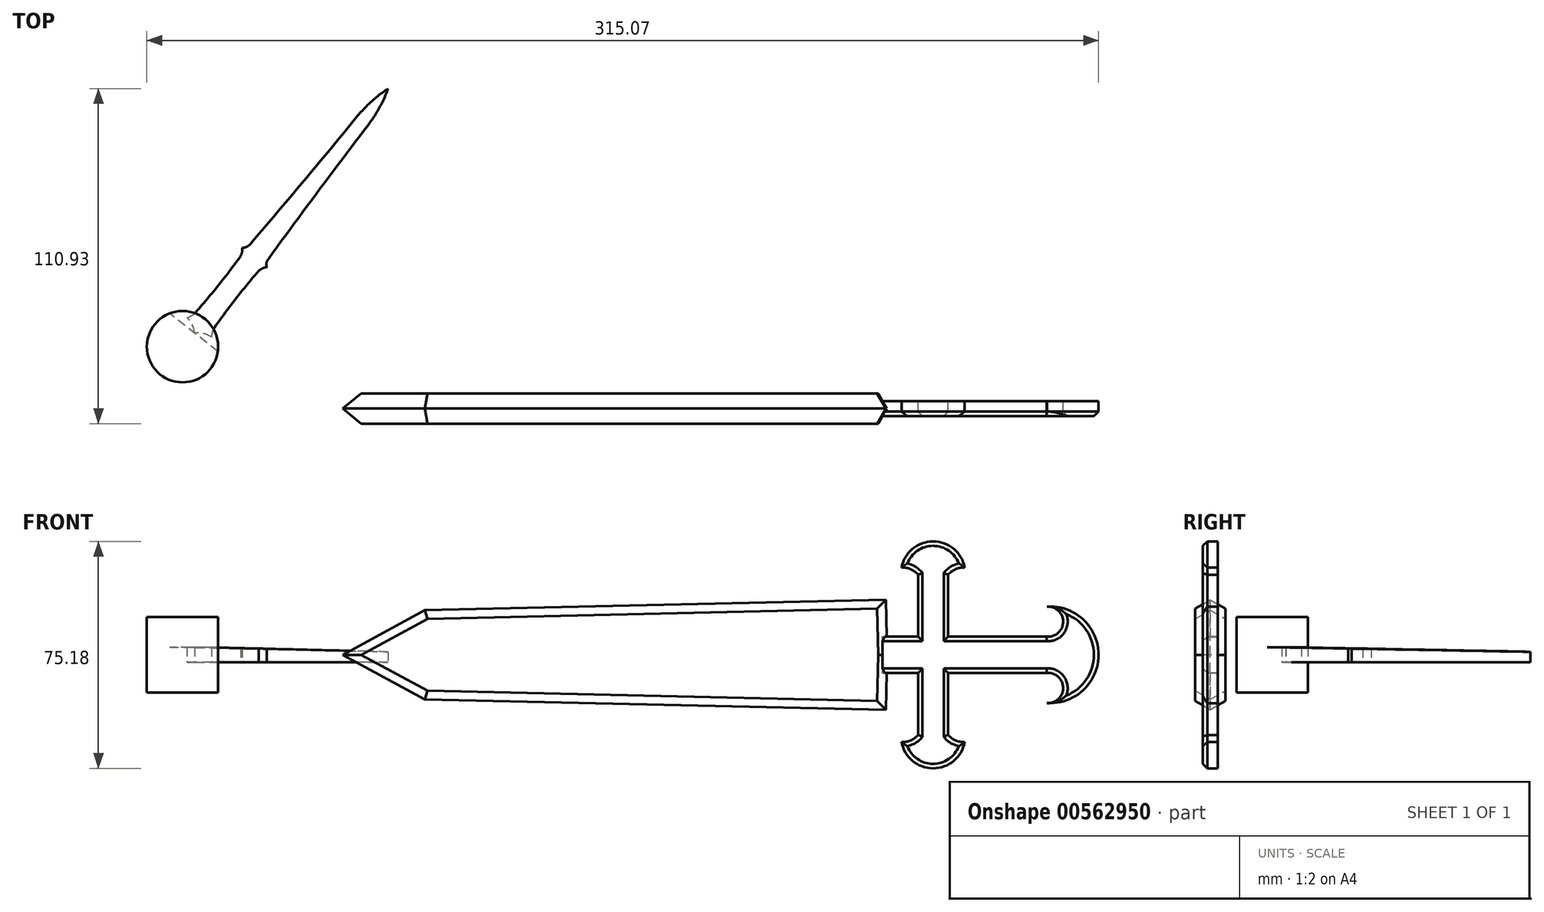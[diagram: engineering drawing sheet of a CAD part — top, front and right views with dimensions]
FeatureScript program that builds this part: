
annotation { "Feature Type Name" : "Feature", "Feature Type Description" : "" }
export const myFeature = defineFeature(function(context is Context, id is Id, definition is map)
    precondition{}
    {
        {
            var Q0;
            Q0=qCreatedBy(makeId("Front.planeOp"),FACE);
            var sketch = newSketch(context, id + "F0", { "sketchPlane" : qUnion([Q0])});
            skLineSegment(sketch, "E0", {"start": v(0, 0) * mm, "end": v(250, 0) * mm, "construction": true});
            skLineSegment(sketch, "E1", {"start": v(0, 0) * mm, "end": v(27.2, 14.78) * mm});
            skLineSegment(sketch, "E2", {"start": v(27.2, 14.78) * mm, "end": v(179.74, 18.21) * mm});
            skLineSegment(sketch, "E3", {"start": v(179.74, 18.21) * mm, "end": v(180.15, 0) * mm});
            skLineSegment(sketch, "E4.MirrorCS", {"start": v(0, 0) * mm, "end": v(27.2, -14.78) * mm});
            skLineSegment(sketch, "E5.MirrorCS", {"start": v(27.2, -14.78) * mm, "end": v(179.74, -18.21) * mm});
            skLineSegment(sketch, "E6.MirrorCS", {"start": v(179.74, -18.21) * mm, "end": v(180.15, 0) * mm});
            skSolve(sketch);
        }
        {
            var Q0;
            Q0=makeQuery(id+"F0.imprint","IMPRINT",FACE,{"disambiguationData":[TD([[makeQuery(id+"F0.imprint","IMPRINT",EDGE,{"derivedFrom":sQuery(id+"F0.wireOp",EDGE,"E1")}),-1.0]])]});
            extrude(context, id + "F1", {"entities" : qUnion([Q0]), "endBound" : BoundingType.SYMMETRIC, "depth" : 10 * mm, "offsetDistance" : 25 * mm, "hasDraft" : true, "draftAngle" : 30 * degree, "draftPullDirection" : true});
        }
        {
            var Q0;
            Q0=qCreatedBy(makeId("Front.planeOp"),FACE);
            var sketch = newSketch(context, id + "F2", { "sketchPlane" : qUnion([Q0])});
            skLineSegment(sketch, "E7", {"start": v(0, 0) * mm, "end": v(460.23, 0) * mm, "construction": true});
            skLineSegment(sketch, "E8", {"start": v(177.13, 6) * mm, "end": v(190.4, 6) * mm});
            skLineSegment(sketch, "E9", {"start": v(190.4, 6) * mm, "end": v(190.4, 26.53) * mm});
            skLineSegment(sketch, "E10", {"start": v(200.4, 26.53) * mm, "end": v(200.4, 6) * mm});
            skLineSegment(sketch, "E11", {"start": v(200.4, 6) * mm, "end": v(233.04, 6) * mm});
            skLineSegment(sketch, "E12", {"start": v(190.4, 6) * mm, "end": v(200.4, 6) * mm, "construction": true});
            skLineSegment(sketch, "E13", {"start": v(195.4, 6) * mm, "end": v(195.4, 44.93) * mm, "construction": true});
            skArc(sketch, "E14", {"start": v(190.4, 26.53) * mm, "mid": v(187.95, 28.36) * mm, "end": v(184.94, 28.88) * mm});
            skArc(sketch, "E15", {"start": v(195.4, 37.6) * mm, "mid": v(188.6, 35.13) * mm, "end": v(184.94, 28.88) * mm});
            skLineSegment(sketch, "E16", {"start": v(195.4, 37.6) * mm, "end": v(213.75, 37.6) * mm, "construction": true});
            skArc(sketch, "E17.MirrorCS", {"start": v(195.4, 37.6) * mm, "mid": v(202.22, 35.13) * mm, "end": v(205.88, 28.88) * mm});
            skArc(sketch, "E18.MirrorCS", {"start": v(200.4, 26.53) * mm, "mid": v(202.86, 28.36) * mm, "end": v(205.88, 28.88) * mm});
            skArc(sketch, "E19", {"start": v(233.04, 6) * mm, "mid": v(238.45, 10.94) * mm, "end": v(233.13, 15.97) * mm});
            skArc(sketch, "E20", {"start": v(250.17, 0) * mm, "mid": v(245.1, 11.68) * mm, "end": v(233.13, 15.97) * mm});
            skLineSegment(sketch, "E21", {"start": v(250.17, 0) * mm, "end": v(250.17, -32.65) * mm, "construction": true});
            skArc(sketch, "E22.MirrorCS", {"start": v(233.04, -6) * mm, "mid": v(238.45, -10.94) * mm, "end": v(233.13, -15.97) * mm});
            skArc(sketch, "E23.MirrorCS", {"start": v(250.17, 0) * mm, "mid": v(245.1, -11.68) * mm, "end": v(233.13, -15.97) * mm});
            skLineSegment(sketch, "E24.MirrorCS", {"start": v(200.4, -6) * mm, "end": v(233.04, -6) * mm});
            skLineSegment(sketch, "E25.MirrorCS", {"start": v(200.4, -26.53) * mm, "end": v(200.4, -6) * mm});
            skArc(sketch, "E26.MirrorCS", {"start": v(200.4, -26.53) * mm, "mid": v(202.86, -28.36) * mm, "end": v(205.88, -28.88) * mm});
            skArc(sketch, "E27.MirrorCS", {"start": v(195.4, -37.6) * mm, "mid": v(202.22, -35.13) * mm, "end": v(205.88, -28.88) * mm});
            skArc(sketch, "E28.MirrorCS", {"start": v(195.4, -37.6) * mm, "mid": v(188.6, -35.13) * mm, "end": v(184.94, -28.88) * mm});
            skArc(sketch, "E29.MirrorCS", {"start": v(190.4, -26.53) * mm, "mid": v(187.95, -28.36) * mm, "end": v(184.94, -28.88) * mm});
            skLineSegment(sketch, "E30.MirrorCS", {"start": v(190.4, -6) * mm, "end": v(190.4, -26.53) * mm});
            skLineSegment(sketch, "E31.MirrorCS", {"start": v(177.13, -6) * mm, "end": v(190.4, -6) * mm});
            skLineSegment(sketch, "E32.0", {"start": v(177.13, 6) * mm, "end": v(177.26, 0) * mm});
            skLineSegment(sketch, "E33.0", {"start": v(177.13, -6) * mm, "end": v(177.26, 0) * mm});
            skPoint(sketch, "E34.orphan", {"position": v(176.92, 15.26) * mm});
            skPoint(sketch, "E35.orphan", {"position": v(176.92, -15.26) * mm});
            skSolve(sketch);
        }
        {
            var Q0;
            Q0 = qSketchRegion(id + "F2", true);
            extrude(context, id + "F3", {"entities" : qUnion([Q0]), "operationType" : NewBodyOperationType.ADD, "endBound" : BoundingType.SYMMETRIC, "depth" : 5 * mm, "offsetDistance" : 25 * mm});
        }
        {
            var Q0;
            Q0=makeQuery(id+"F3.opExtrude","CAP_EDGE",EDGE,{"disambiguationData":[OSD([sQuery(id+"F2.wireOp",EDGE,"E15"),sQuery(id+"F2.wireOp",EDGE,"E17.MirrorCS")])],"isStart":false});
            var Q1;
            Q1=makeQuery(id+"F3.opExtrude","CAP_EDGE",EDGE,{"disambiguationData":[OSD([sQuery(id+"F2.wireOp",EDGE,"E18.MirrorCS")])],"isStart":false});
            var Q2;
            Q2=makeQuery(id+"F3.opExtrude","CAP_EDGE",EDGE,{"disambiguationData":[OSD([sQuery(id+"F2.wireOp",EDGE,"E14")])],"isStart":false});
            var Q3;
            Q3=makeQuery(id+"F3.opExtrude","CAP_EDGE",EDGE,{"disambiguationData":[OSD([sQuery(id+"F2.wireOp",EDGE,"E19")])],"isStart":false});
            var Q4;
            Q4=makeQuery(id+"F3.opExtrude","CAP_EDGE",EDGE,{"disambiguationData":[OSD([sQuery(id+"F2.wireOp",EDGE,"E20"),sQuery(id+"F2.wireOp",EDGE,"E23.MirrorCS")])],"isStart":false});
            var Q5;
            Q5=makeQuery(id+"F3.opExtrude","CAP_EDGE",EDGE,{"disambiguationData":[OSD([sQuery(id+"F2.wireOp",EDGE,"E22.MirrorCS")])],"isStart":false});
            var Q6;
            Q6=makeQuery(id+"F3.opExtrude","CAP_EDGE",EDGE,{"disambiguationData":[OSD([sQuery(id+"F2.wireOp",EDGE,"E24.MirrorCS")])],"isStart":false});
            var Q7;
            Q7=makeQuery(id+"F3.opExtrude","CAP_EDGE",EDGE,{"disambiguationData":[OSD([sQuery(id+"F2.wireOp",EDGE,"E11")])],"isStart":false});
            var Q8;
            Q8=makeQuery(id+"F3.opExtrude","CAP_EDGE",EDGE,{"disambiguationData":[OSD([sQuery(id+"F2.wireOp",EDGE,"E10")])],"isStart":false});
            var Q9;
            Q9=makeQuery(id+"F3.opExtrude","CAP_EDGE",EDGE,{"disambiguationData":[OSD([sQuery(id+"F2.wireOp",EDGE,"E9")])],"isStart":false});
            var Q10;
            Q10=makeQuery(id+"F3.opExtrude","CAP_EDGE",EDGE,{"disambiguationData":[OSD([sQuery(id+"F2.wireOp",EDGE,"E8")])],"isStart":false});
            var Q11;
            Q11=makeQuery(id+"F3.opExtrude","CAP_EDGE",EDGE,{"disambiguationData":[OSD([sQuery(id+"F2.wireOp",EDGE,"E31.MirrorCS")])],"isStart":false});
            var Q12;
            Q12=makeQuery(id+"F3.opExtrude","CAP_EDGE",EDGE,{"disambiguationData":[OSD([sQuery(id+"F2.wireOp",EDGE,"E30.MirrorCS")])],"isStart":false});
            var Q13;
            Q13=makeQuery(id+"F3.opExtrude","CAP_EDGE",EDGE,{"disambiguationData":[OSD([sQuery(id+"F2.wireOp",EDGE,"E25.MirrorCS")])],"isStart":false});
            var Q14;
            Q14=makeQuery(id+"F3.opExtrude","CAP_EDGE",EDGE,{"disambiguationData":[OSD([sQuery(id+"F2.wireOp",EDGE,"E26.MirrorCS")])],"isStart":false});
            var Q15;
            Q15=makeQuery(id+"F3.opExtrude","CAP_EDGE",EDGE,{"disambiguationData":[OSD([sQuery(id+"F2.wireOp",EDGE,"E29.MirrorCS")])],"isStart":false});
            var Q16;
            Q16=makeQuery(id+"F3.opExtrude","CAP_EDGE",EDGE,{"disambiguationData":[OSD([sQuery(id+"F2.wireOp",EDGE,"E27.MirrorCS"),sQuery(id+"F2.wireOp",EDGE,"E28.MirrorCS")])],"isStart":false});
            chamfer(context, id + "F4", {"entities" : qUnion([Q0, Q1, Q2, Q3, Q4, Q5, Q6, Q7, Q8, Q9, Q10, Q11, Q12, Q13, Q14, Q15, Q16]), "width" : 1.5 * mm, "tangentPropagation" : true});
        }
        {
            var Q0;
            Q0=qCreatedBy(makeId("Top.planeOp"),FACE);
            var sketch = newSketch(context, id + "F5", { "sketchPlane" : qUnion([Q0])});
            skLineSegment(sketch, "E36", {"start": v(-78.1, -11.73) * mm, "end": v(14.94, 105.93) * mm});
            skArc(sketch, "E37", {"start": v(14.94, 105.93) * mm, "mid": v(9.61, 101.85) * mm, "end": v(4.97, 97) * mm});
            skArc(sketch, "E38", {"start": v(-30.83, 54.31) * mm, "mid": v(-12.8, 75.55) * mm, "end": v(4.97, 97) * mm});
            skArc(sketch, "E39", {"start": v(-33.32, 53.27) * mm, "mid": v(-31.95, 53.5) * mm, "end": v(-30.83, 54.31) * mm});
            skArc(sketch, "E40", {"start": v(-33.87, 50.44) * mm, "mid": v(-33.38, 51.81) * mm, "end": v(-33.32, 53.27) * mm});
            skArc(sketch, "E41", {"start": v(-48.8, 31.8) * mm, "mid": v(-41.1, 40.92) * mm, "end": v(-33.87, 50.44) * mm});
            skArc(sketch, "E42", {"start": v(-51.64, 30.11) * mm, "mid": v(-50.1, 30.74) * mm, "end": v(-48.8, 31.8) * mm});
            skArc(sketch, "E43.MirrorCS", {"start": v(14.94, 105.93) * mm, "mid": v(12.2, 99.8) * mm, "end": v(8.55, 94.17) * mm});
            skArc(sketch, "E44.MirrorCS", {"start": v(-24.73, 49.5) * mm, "mid": v(-8.22, 71.92) * mm, "end": v(8.55, 94.17) * mm});
            skArc(sketch, "E45.MirrorCS", {"start": v(-25.17, 46.83) * mm, "mid": v(-25.27, 48.21) * mm, "end": v(-24.73, 49.5) * mm});
            skArc(sketch, "E46.MirrorCS", {"start": v(-27.8, 45.64) * mm, "mid": v(-26.58, 46.43) * mm, "end": v(-25.17, 46.83) * mm});
            skArc(sketch, "E47.MirrorCS", {"start": v(-42.5, 26.8) * mm, "mid": v(-35.4, 36.42) * mm, "end": v(-27.8, 45.64) * mm});
            skArc(sketch, "E48.MirrorCS", {"start": v(-43.48, 23.66) * mm, "mid": v(-43.23, 25.3) * mm, "end": v(-42.5, 26.8) * mm});
            skArc(sketch, "E49", {"start": v(-49.09, 24.96) * mm, "mid": v(-49.89, 27.77) * mm, "end": v(-51.64, 30.11) * mm});
            skArc(sketch, "E50.MirrorCS", {"start": v(-49.09, 24.96) * mm, "mid": v(-46.16, 24.83) * mm, "end": v(-43.48, 23.66) * mm});
            skSolve(sketch);
        }
        {
            var Q0;
            Q0 = qSketchRegion(id + "F5", true);
            extrude(context, id + "F6", {"entities" : qUnion([Q0]), "endBound" : BoundingType.SYMMETRIC, "depth" : 5 * mm, "offsetDistance" : 25 * mm});
        }
        {
            var Q0;
            Q0=qCreatedBy(makeId("Top.planeOp"),FACE);
            var sketch = newSketch(context, id + "F7", { "sketchPlane" : qUnion([Q0])});
            skCircle(sketch, "E51", {"center": v(-53.08, 20.49) * mm, "radius": 11.82 * mm});
            skSolve(sketch);
        }
        {
            var Q0;
            Q0 = qSketchRegion(id + "F7", true);
            extrude(context, id + "F8", {"entities" : qUnion([Q0]), "endBound" : BoundingType.SYMMETRIC, "depth" : 25 * mm, "offsetDistance" : 25 * mm});
        }
        {
            var Q0;
            Q0=sQuery(id+"F5.wireOp",EDGE,"E36");
            extrude(context, id + "F9", {"bodyType" : ToolBodyType.SURFACE, "surfaceEntities" : qUnion([Q0]), "endBound" : BoundingType.SYMMETRIC, "depth" : 25 * mm, "offsetDistance" : 25 * mm});
        }
        {
            var Q0;
            Q0=makeQuery(id+"F9.opExtrude","SWEPT_FACE",FACE,{"disambiguationData":[OSD([sQuery(id+"F5.wireOp",EDGE,"E36")])]});
            var sketch = newSketch(context, id + "F10", { "sketchPlane" : qUnion([Q0])});
            skLineSegment(sketch, "E52", {"start": v(-10.87, 2.5) * mm, "end": v(92.36, 1) * mm});
            skLineSegment(sketch, "E53.0", {"start": v(92.36, 2.5) * mm, "end": v(92.36, 1) * mm});
            skPoint(sketch, "E54.orphan", {"position": v(92.36, -2.5) * mm});
            skLineSegment(sketch, "E55", {"start": v(92.36, 2.5) * mm, "end": v(-10.87, 2.5) * mm});
            skSolve(sketch);
        }
        {
            var Q0;
            Q0 = qSketchRegion(id + "F10", true);
            extrude(context, id + "F11", {"entities" : qUnion([Q0]), "operationType" : NewBodyOperationType.REMOVE, "endBound" : BoundingType.SYMMETRIC, "depth" : 25 * mm, "offsetDistance" : 25 * mm});
        }
    });
